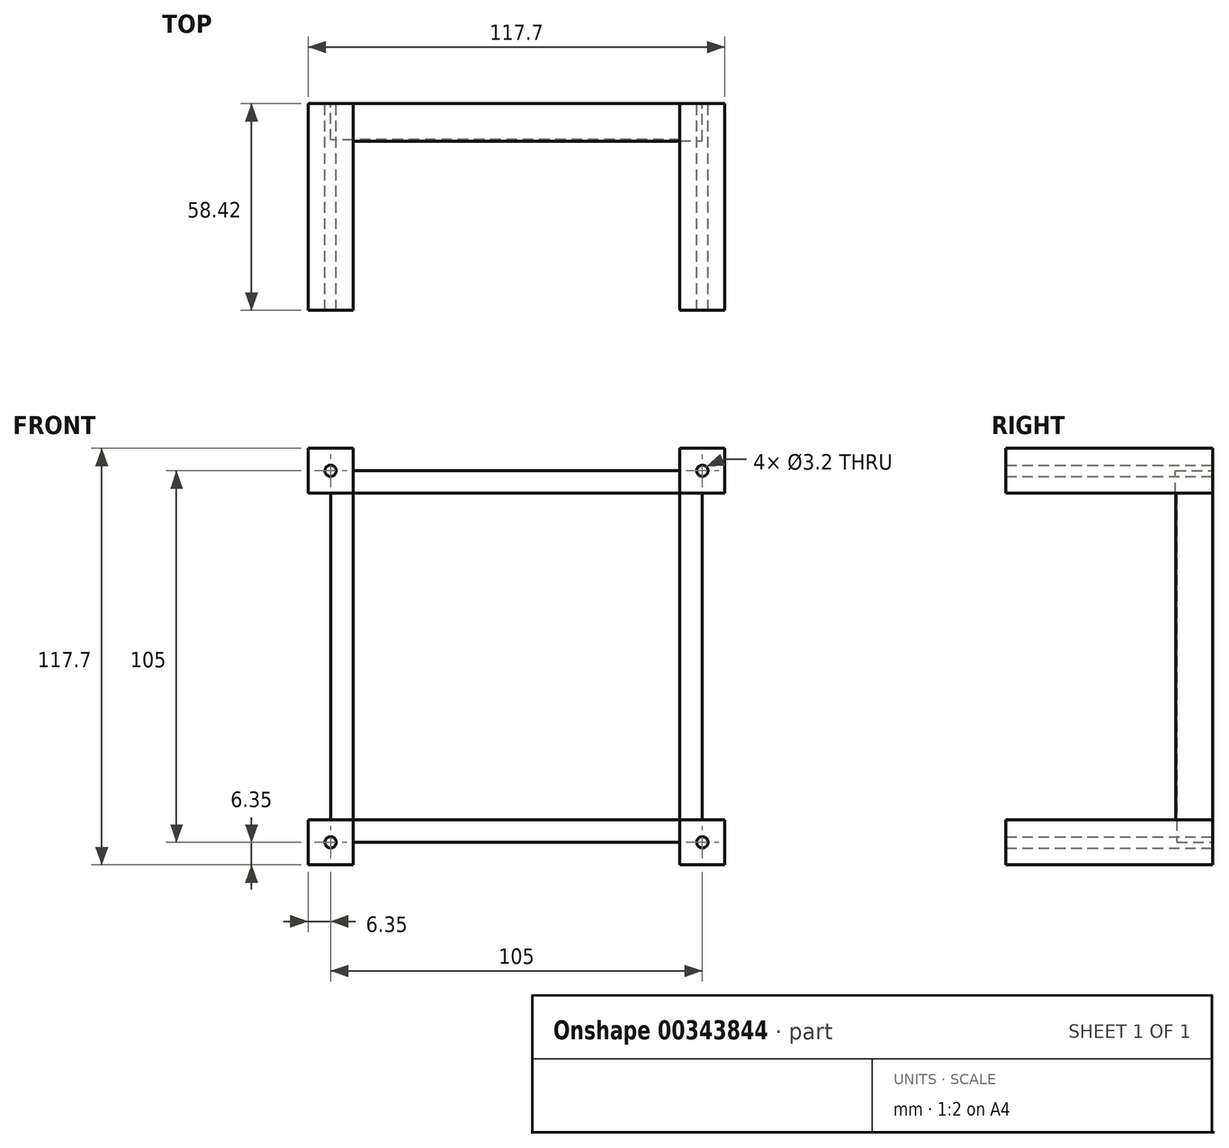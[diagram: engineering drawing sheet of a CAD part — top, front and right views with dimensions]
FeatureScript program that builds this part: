
annotation { "Feature Type Name" : "Feature", "Feature Type Description" : "" }
export const myFeature = defineFeature(function(context is Context, id is Id, definition is map)
    precondition{}
    {
        {
            var Q0;
            Q0=qCreatedBy(makeId("Front.planeOp"),FACE);
            var sketch = newSketch(context, id + "F0", { "sketchPlane" : qUnion([Q0])});
            skLineSegment(sketch, "E0.bottom", {"start": v(-98.65, 111.35) * mm, "end": v(-111.35, 111.35) * mm});
            skLineSegment(sketch, "E0.top", {"start": v(-98.65, 98.65) * mm, "end": v(-111.35, 98.65) * mm});
            skLineSegment(sketch, "E0.left", {"start": v(-98.65, 111.35) * mm, "end": v(-98.65, 98.65) * mm});
            skLineSegment(sketch, "E0.right", {"start": v(-111.35, 111.35) * mm, "end": v(-111.35, 98.65) * mm});
            skPoint(sketch, "E0.middle", {"position": v(-105, 105) * mm});
            skLineSegment(sketch, "E1.bottom", {"start": v(6.35, 111.35) * mm, "end": v(-6.35, 111.35) * mm});
            skLineSegment(sketch, "E1.top", {"start": v(6.35, 98.65) * mm, "end": v(-6.35, 98.65) * mm});
            skLineSegment(sketch, "E1.left", {"start": v(6.35, 111.35) * mm, "end": v(6.35, 98.65) * mm});
            skLineSegment(sketch, "E1.right", {"start": v(-6.35, 111.35) * mm, "end": v(-6.35, 98.65) * mm});
            skPoint(sketch, "E1.middle", {"position": v(0, 105) * mm});
            skLineSegment(sketch, "E2.bottom", {"start": v(6.35, 6.35) * mm, "end": v(-6.35, 6.35) * mm});
            skLineSegment(sketch, "E2.top", {"start": v(6.35, -6.35) * mm, "end": v(-6.35, -6.35) * mm});
            skLineSegment(sketch, "E2.left", {"start": v(6.35, 6.35) * mm, "end": v(6.35, -6.35) * mm});
            skLineSegment(sketch, "E2.right", {"start": v(-6.35, 6.35) * mm, "end": v(-6.35, -6.35) * mm});
            skPoint(sketch, "E2.middle", {"position": v(0, 0) * mm});
            skLineSegment(sketch, "E3.bottom", {"start": v(-98.65, 6.35) * mm, "end": v(-111.35, 6.35) * mm});
            skLineSegment(sketch, "E3.top", {"start": v(-98.65, -6.35) * mm, "end": v(-111.35, -6.35) * mm});
            skLineSegment(sketch, "E3.left", {"start": v(-98.65, 6.35) * mm, "end": v(-98.65, -6.35) * mm});
            skLineSegment(sketch, "E3.right", {"start": v(-111.35, 6.35) * mm, "end": v(-111.35, -6.35) * mm});
            skPoint(sketch, "E3.middle", {"position": v(-105, 0) * mm});
            skLineSegment(sketch, "E4.bottom", {"start": v(-98.65, 98.65) * mm, "end": v(-105, 98.65) * mm});
            skLineSegment(sketch, "E4.top", {"start": v(-98.65, 6.35) * mm, "end": v(-105, 6.35) * mm});
            skLineSegment(sketch, "E4.left", {"start": v(-98.65, 98.65) * mm, "end": v(-98.65, 6.35) * mm});
            skLineSegment(sketch, "E4.right", {"start": v(-105, 98.65) * mm, "end": v(-105, 6.35) * mm});
            skLineSegment(sketch, "E5.bottom", {"start": v(-98.65, 98.65) * mm, "end": v(-6.35, 98.65) * mm});
            skLineSegment(sketch, "E5.top", {"start": v(-98.65, 105) * mm, "end": v(-6.35, 105) * mm});
            skLineSegment(sketch, "E5.left", {"start": v(-98.65, 98.65) * mm, "end": v(-98.65, 105) * mm});
            skLineSegment(sketch, "E5.right", {"start": v(-6.35, 98.65) * mm, "end": v(-6.35, 105) * mm});
            skLineSegment(sketch, "E6.bottom", {"start": v(-6.35, 98.65) * mm, "end": v(0, 98.65) * mm});
            skLineSegment(sketch, "E6.top", {"start": v(-6.35, 0) * mm, "end": v(0, 0) * mm});
            skLineSegment(sketch, "E6.left", {"start": v(-6.35, 98.65) * mm, "end": v(-6.35, 0) * mm});
            skLineSegment(sketch, "E6.right", {"start": v(0, 98.65) * mm, "end": v(0, 0) * mm});
            skLineSegment(sketch, "E7.bottom", {"start": v(-6.35, 0) * mm, "end": v(-98.65, 0) * mm});
            skLineSegment(sketch, "E7.top", {"start": v(-6.35, 6.35) * mm, "end": v(-98.65, 6.35) * mm});
            skLineSegment(sketch, "E7.left", {"start": v(-6.35, 0) * mm, "end": v(-6.35, 6.35) * mm});
            skLineSegment(sketch, "E7.right", {"start": v(-98.65, 0) * mm, "end": v(-98.65, 6.35) * mm});
            skCircle(sketch, "E8", {"center": v(0, 105) * mm, "radius": 1.6 * mm});
            skCircle(sketch, "E9", {"center": v(-105, 105) * mm, "radius": 1.6 * mm});
            skCircle(sketch, "E10", {"center": v(-105, 0) * mm, "radius": 1.6 * mm});
            skCircle(sketch, "E11", {"center": v(0, 0) * mm, "radius": 1.6 * mm});
            skSolve(sketch);
        }
        {
            var Q0;
            Q0 = qSketchRegion(id + "F0", true);
            extrude(context, id + "F1", {"entities" : qUnion([Q0]), "depth" : 58.42 * mm});
        }
        {
            var Q0;
            Q0=makeQuery(id+"F1.opExtrude","SWEPT_FACE",FACE,{"disambiguationData":[OSD([sQuery(id+"F0.wireOp",EDGE,"E4.right")])]});
            var sketch = newSketch(context, id + "F2", { "sketchPlane" : qUnion([Q0])});
            skLineSegment(sketch, "E12.bottom", {"start": v(58.42, 98.65) * mm, "end": v(10.25, 98.65) * mm});
            skLineSegment(sketch, "E12.top", {"start": v(58.42, 6.35) * mm, "end": v(10.25, 6.35) * mm});
            skLineSegment(sketch, "E12.left", {"start": v(58.42, 98.65) * mm, "end": v(58.42, 6.35) * mm});
            skLineSegment(sketch, "E12.right", {"start": v(10.25, 98.65) * mm, "end": v(10.25, 6.35) * mm});
            skSolve(sketch);
        }
        {
            var Q0;
            Q0=makeQuery(id+"F2.imprint","IMPRINT",FACE,{"disambiguationData":[TD([[makeQuery(id+"F2.imprint","IMPRINT",EDGE,{"derivedFrom":sQuery(id+"F2.wireOp",EDGE,"E12.bottom")}),1.0]])]});
            extrude(context, id + "F3", {"entities" : qUnion([Q0]), "operationType" : NewBodyOperationType.REMOVE, "oppositeDirection" : true, "depth" : 25.4 * mm});
        }
        {
            var Q0;
            Q0=makeQuery(id+"F1.opExtrude","SWEPT_FACE",FACE,{"disambiguationData":[OSD([sQuery(id+"F0.wireOp",EDGE,"E7.bottom")])]});
            var sketch = newSketch(context, id + "F4", { "sketchPlane" : qUnion([Q0])});
            skLineSegment(sketch, "E13.bottom", {"start": v(-6.35, 58.42) * mm, "end": v(-98.65, 58.42) * mm});
            skLineSegment(sketch, "E13.top", {"start": v(-6.35, 10.15) * mm, "end": v(-98.65, 10.15) * mm});
            skLineSegment(sketch, "E13.left", {"start": v(-6.35, 58.42) * mm, "end": v(-6.35, 10.15) * mm});
            skLineSegment(sketch, "E13.right", {"start": v(-98.65, 58.42) * mm, "end": v(-98.65, 10.15) * mm});
            skSolve(sketch);
        }
        {
            var Q0;
            Q0 = qSketchRegion(id + "F4", true);
            extrude(context, id + "F5", {"entities" : qUnion([Q0]), "operationType" : NewBodyOperationType.REMOVE, "oppositeDirection" : true, "depth" : 25.4 * mm});
        }
        {
            var Q0;
            Q0=makeQuery(id+"F1.opExtrude","SWEPT_FACE",FACE,{"disambiguationData":[OSD([sQuery(id+"F0.wireOp",EDGE,"E6.right")])]});
            var sketch = newSketch(context, id + "F6", { "sketchPlane" : qUnion([Q0])});
            skLineSegment(sketch, "E14.bottom", {"start": v(-58.42, 98.65) * mm, "end": v(-10.52, 98.65) * mm});
            skLineSegment(sketch, "E14.top", {"start": v(-58.42, 6.35) * mm, "end": v(-10.52, 6.35) * mm});
            skLineSegment(sketch, "E14.left", {"start": v(-58.42, 98.65) * mm, "end": v(-58.42, 6.35) * mm});
            skLineSegment(sketch, "E14.right", {"start": v(-10.52, 98.65) * mm, "end": v(-10.52, 6.35) * mm});
            skSolve(sketch);
        }
        {
            var Q0;
            Q0 = qSketchRegion(id + "F6", true);
            extrude(context, id + "F7", {"entities" : qUnion([Q0]), "operationType" : NewBodyOperationType.REMOVE, "oppositeDirection" : true, "depth" : 25.4 * mm});
        }
        {
            var Q0;
            Q0=makeQuery(id+"F1.opExtrude","SWEPT_FACE",FACE,{"disambiguationData":[OSD([sQuery(id+"F0.wireOp",EDGE,"E5.top")])]});
            var sketch = newSketch(context, id + "F8", { "sketchPlane" : qUnion([Q0])});
            skLineSegment(sketch, "E15.bottom", {"start": v(-98.65, -58.42) * mm, "end": v(-6.35, -58.42) * mm});
            skLineSegment(sketch, "E15.top", {"start": v(-98.65, -10.58) * mm, "end": v(-6.35, -10.58) * mm});
            skLineSegment(sketch, "E15.left", {"start": v(-98.65, -58.42) * mm, "end": v(-98.65, -10.58) * mm});
            skLineSegment(sketch, "E15.right", {"start": v(-6.35, -58.42) * mm, "end": v(-6.35, -10.58) * mm});
            skSolve(sketch);
        }
        {
            var Q0;
            Q0 = qSketchRegion(id + "F8", true);
            extrude(context, id + "F9", {"entities" : qUnion([Q0]), "operationType" : NewBodyOperationType.REMOVE, "oppositeDirection" : true, "depth" : 25.4 * mm});
        }
    });
